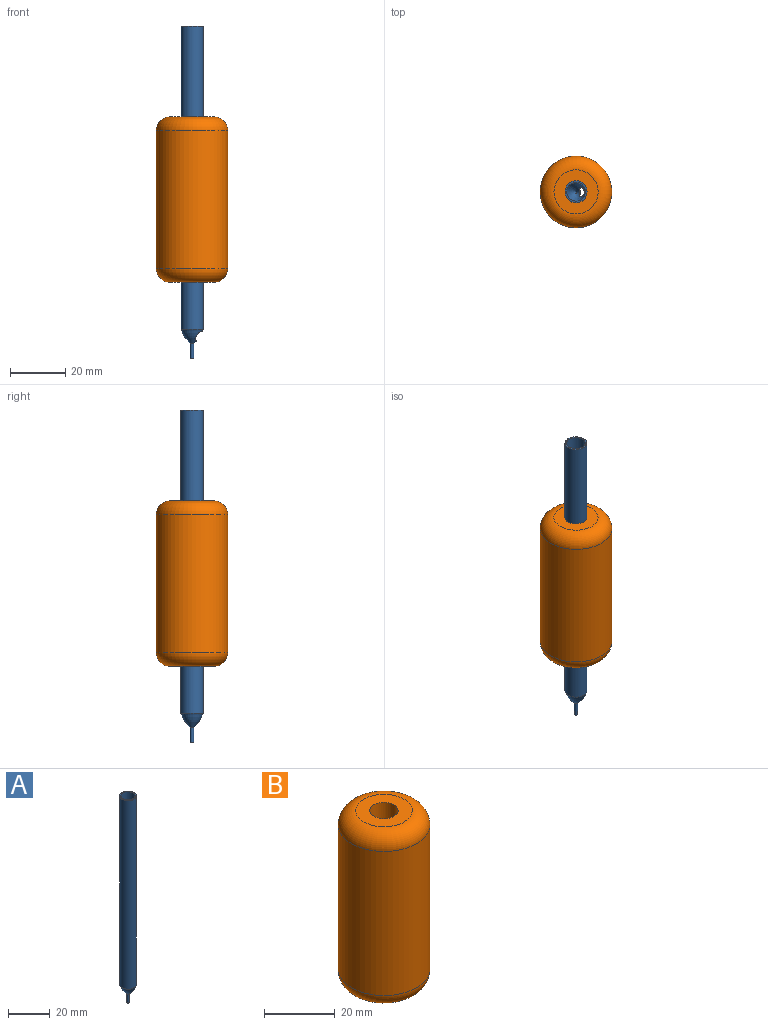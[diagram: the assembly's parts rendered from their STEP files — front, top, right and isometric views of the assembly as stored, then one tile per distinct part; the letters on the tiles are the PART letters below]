
ASSEMBLY  parts=2 mates=1
PART A: 8 faces, bbox 8x8x120.5 mm
  f0: revolved ~8x8mm, area 8.7mm2, adj f4,f5,f7
  f1: revolved ~6.8x6.8mm, area 66.4mm2, adj f2,f7
  f2: cylinder r=3.4mm len=110mm, axis (0,0,1), area 2349.9mm2, adj f1,f3
  f3: plane 8x8mm, normal (0,0,1), area 13.9mm2, adj f2,f4
  f4: cylinder r=4mm len=110mm, axis (0,0,1), area 2764.6mm2, adj f0,f3
  f5: cylinder r=0.6mm len=5.22mm, axis (0,0,1), area 19.7mm2, adj f0,f6
  f6: cone r=0.6mm half-angle=85.9deg, axis (0,0,-1), area 1.1mm2, adj f5
  f7: extruded ~5.21x3.57mm, area 9.7mm2, adj f0,f1
PART B: 6 faces, bbox 28.1x28.1x60 mm
  f0: plane 16x16mm, normal (0,0,1), area 150.8mm2, adj f3,f4
  f1: cylinder r=13mm len=50mm, axis (0,0,1), area 4084.1mm2, adj f4,f5
  f2: plane 16x16mm, normal (0,0,-1), area 150.8mm2, adj f3,f5
  f3: cylinder r=4mm len=60mm, axis (0,0,1), area 1508mm2, adj f0,f2
  f4: torus R=8mm, axis (0,0,-1), area 551.9mm2, adj f0,f1
  f5: torus R=8mm, axis (0,0,-1), area 551.9mm2, adj f1,f2
PLACE A t=(-30.86,13.16,9.05)mm
PLACE B t=(5.78,13.16,18.5)mm
MATE cylindrical A.f2 <-> B.f1  axis (0,0,1) through (-31.46,13.16,54.83)mm
